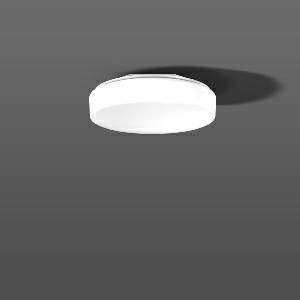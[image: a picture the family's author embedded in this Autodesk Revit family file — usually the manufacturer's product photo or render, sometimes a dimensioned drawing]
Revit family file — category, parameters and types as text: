
# Revit family: flat_polymero_kreis_672092_002_8_1_04_a6bf
name_source: partatom
category: Lighting Fixtures
units: mm (PartAtom-declared; Revit-internal decimal feet)

## family parameters
Cut with Voids When Loaded = No
Host = Face
Light Source = No
Part Type = Normal
Room Calculation Point = No
Round Connector Dimension = Use Diameter
Shared = No

## types (1)
- FLAT POLYMERO KREIS (1 x LED Modul 830, 1750 lm, 3000)
    Apparent Load = 15 VA
    CIE Flux Codes = 43 73 91 87 100
    Color Rendering = 80
    Color Temperature = 3000
    Default Elevation = 1800 mm
    Description = Series: FLAT POLYMERO KREIS
Decorative round surface-mounted luminaire. For escape route illumination. Base: metal, powder-coated. Diffuser made of plastic (polycarbonate), opal, shockproof. Diffuser fastening: patented push system. Suitable for Ceiling mounting, Wall (surface). Self-contained system with automatic self-test and feedback to the RZB monitoring system MULTIDIGIT. 
Colour: white
Diameter: 360 mm
Height: 109 mm
Weight: 1.88 kg
Operating mode: Combined NL readiness
Duration time: 3 h
Lamp: LED
Socket: without socket
Colour temperature: 3000K
Colour rendering index (CRI): 80
System power: 15 W
Rated luminous flux: 1750 lm
Luminous flux, emergency: 200 lm
System power, emergency: -
Control gear: Regulated power supply
Protection class: I
Type of protection: IP 40
    Height = 109 mm
    Lamp = 1 x LED Modul 830
    Lamp Light Flux = 1750 lm
    Lamp count = 1
    Length = 360 mm
    Lifetime = 50000 h
    Luminous efficacy = 117 lm/W
    Manufacturer = RZB
    ModVariant = No
    Model = 672092.002.8.1.04
    Mounting Place = Ceiling
    Mounting Type = Surface mounted
    Number of Poles = 1
    OnlyDefault = Yes
    Power Factor = 1
    Product Name = FLAT POLYMERO KREIS
    Product group = Surface mounted ceiling and wall luminaires
    ProductGroupID = 305
    Protection Class = Protection class I
    Protection Degree = Degree of protection
    RLX_Detail_Level = 1
    RLX_Emergency_Light_Flux = 200 lm
    RLX_Emergency_Type = 3
    RLX_Emergency_Type_DB = Yes
    RlxData = <blob elided: 51721 chars, md5=71c0c541>
    Socket = socket
    Standby Power = 0 W
    System Light Flux = 1750 lm
    System Power = 15 W
    Type Comments = Product without accessories
    Type Image = 672092.002.1.jpg
    URL = http://relux.com
    VarID = ---
    Voltage = 0 V
    Weight = 0.00 kg
    Width = 0 mm  [stored 0 ft]

note: [stored X ft] marks values corroborated as IEEE doubles in the binary element streams (Revit-internal decimal feet)

## geometry (parser evidence)
native form markers: Blend x4, Sweep x16
no freeform markers — native parametric forms only
